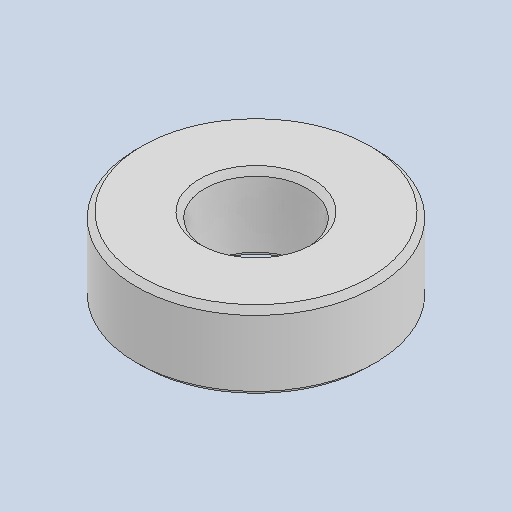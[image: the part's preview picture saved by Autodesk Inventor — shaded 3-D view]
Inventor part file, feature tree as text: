
AUTODESK INVENTOR PART (.ipt)
format: ipt  version: 2022.3 (Build 263350000, 350)  size: 98,304 bytes
history: native  units: in
note: dims shown in document units (in); Inventor stores cm internally (conversion verified against a paired STEP export)
features: chamfer x1
ambient origin geometry x8: Origin, YZ Plane, XZ Plane, XY Plane, X Axis, Y Axis, Z Axis, Center Point
bodies: Solid1 (feature_tree)
feature tree (1):
  chamfer  "Chamfer1"  [1 undecoded]
note: 1 required parameter value undecoded (feature->parameter linkage not recoverable at this tier; creation-order binding heuristic only, values carry confidence <= 0.55)
